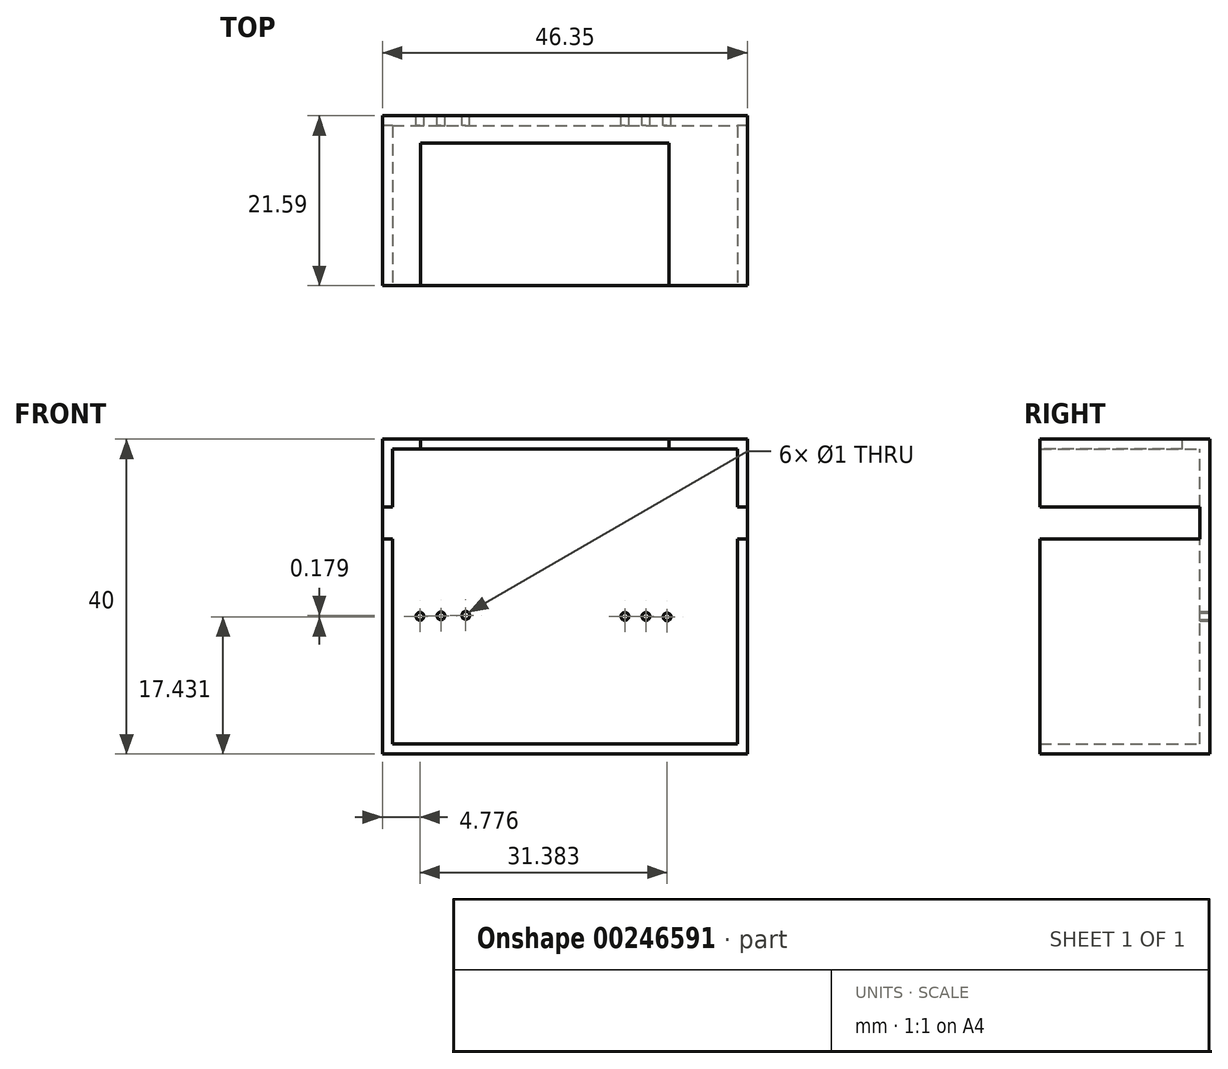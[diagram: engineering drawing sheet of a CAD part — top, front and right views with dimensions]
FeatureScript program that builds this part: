
annotation { "Feature Type Name" : "Feature", "Feature Type Description" : "" }
export const myFeature = defineFeature(function(context is Context, id is Id, definition is map)
    precondition{}
    {
        {
            var Q0;
            Q0=qCreatedBy(makeId("Front.planeOp"),FACE);
            var sketch = newSketch(context, id + "F0", { "sketchPlane" : qUnion([Q0])});
            skLineSegment(sketch, "E0.bottom", {"start": v(0, 0) * mm, "end": v(46.35, 0) * mm});
            skLineSegment(sketch, "E0.top", {"start": v(0, 40) * mm, "end": v(46.35, 40) * mm});
            skLineSegment(sketch, "E0.left", {"start": v(0, 0) * mm, "end": v(0, 40) * mm});
            skLineSegment(sketch, "E0.right", {"start": v(46.35, 0) * mm, "end": v(46.35, 40) * mm});
            skSolve(sketch);
        }
        {
            var Q0;
            Q0 = qSketchRegion(id + "F0", true);
            extrude(context, id + "F1", {"entities" : qUnion([Q0]), "depth" : 21.59 * mm});
        }
        {
            var Q0;
            Q0=makeQuery(id+"F1.opExtrude","CAP_FACE",FACE,{"disambiguationData":[OSD([sQuery(id+"F0.wireOp",EDGE,"E0.bottom"),sQuery(id+"F0.wireOp",EDGE,"E0.top"),sQuery(id+"F0.wireOp",EDGE,"E0.left"),sQuery(id+"F0.wireOp",EDGE,"E0.right")])],"isStart":true});
            var sketch = newSketch(context, id + "F2", { "sketchPlane" : qUnion([Q0])});
            skSolve(sketch);
        }
        {
            var Q0;
            Q0=makeQuery(id+"F1.opExtrude","CAP_FACE",FACE,{"disambiguationData":[OSD([sQuery(id+"F0.wireOp",EDGE,"E0.bottom"),sQuery(id+"F0.wireOp",EDGE,"E0.top"),sQuery(id+"F0.wireOp",EDGE,"E0.left"),sQuery(id+"F0.wireOp",EDGE,"E0.right")])],"isStart":false});
            shell(context, id + "F3", {"entities" : qUnion([Q0]), "thickness" : 1.27 * mm});
        }
        {
            var Q0;
            Q0=makeQuery(id+"F2.imprint","IMPRINT",FACE,{"disambiguationData":[TD([[makeQuery(id+"F2.imprint","IMPRINT",EDGE,{"derivedFrom":makeQuery(id+"F1.opExtrude","CAP_EDGE",EDGE,{"disambiguationData":[OSD([sQuery(id+"F0.wireOp",EDGE,"E0.bottom")])],"isStart":true})}),-1.0]])]});
            var sketch = newSketch(context, id + "F4", { "sketchPlane" : qUnion([Q0])});
            skPoint(sketch, "E1", {"position": v(-20.64, 22.54) * mm});
            skSolve(sketch);
        }
        {
            var Q0;
            Q0=qCreatedBy(makeId("Right.planeOp"),FACE);
            var sketch = newSketch(context, id + "F5", { "sketchPlane" : qUnion([Q0])});
            skLineSegment(sketch, "E2.bottom", {"start": v(-1.27, 31.4) * mm, "end": v(-28.2, 31.4) * mm});
            skLineSegment(sketch, "E2.top", {"start": v(-1.27, 27.34) * mm, "end": v(-28.2, 27.34) * mm});
            skLineSegment(sketch, "E2.left", {"start": v(-1.27, 31.4) * mm, "end": v(-1.27, 27.34) * mm});
            skLineSegment(sketch, "E2.right", {"start": v(-28.2, 31.4) * mm, "end": v(-28.2, 27.34) * mm});
            skSolve(sketch);
        }
        {
            var Q0;
            Q0=makeQuery(id+"F5.imprint","IMPRINT",FACE,{"disambiguationData":[TD([[makeQuery(id+"F5.imprint","IMPRINT",EDGE,{"derivedFrom":sQuery(id+"F5.wireOp",EDGE,"E2.bottom")}),1.0]])]});
            extrude(context, id + "F6", {"entities" : qUnion([Q0]), "operationType" : NewBodyOperationType.REMOVE, "depth" : 63.25 * mm});
        }
        {
            var Q0;
            Q0=makeQuery(id+"F4.imprint","IMPRINT",FACE,{"disambiguationData":[TD([[makeQuery(id+"F4.imprint","IMPRINT",EDGE,{"derivedFrom":makeQuery(id+"F2.imprint","IMPRINT",EDGE,{"derivedFrom":makeQuery(id+"F1.opExtrude","CAP_EDGE",EDGE,{"disambiguationData":[OSD([sQuery(id+"F0.wireOp",EDGE,"E0.bottom")])],"isStart":true})})}),-1.0]])]});
            var sketch = newSketch(context, id + "F7", { "sketchPlane" : qUnion([Q0])});
            skPoint(sketch, "E3", {"position": v(-10.6, 17.6) * mm});
            skSolve(sketch);
        }
        {
            var Q0;
            Q0=sQuery(id+"F7.wireOp",VERTEX,"E3");
            var Q1;
            Q1=makeQuery(id+"F1.opExtrude","SWEPT_BODY",BODY,{"disambiguationData":[OSD([sQuery(id+"F0.wireOp",EDGE,"E0.bottom"),sQuery(id+"F0.wireOp",EDGE,"E0.top"),sQuery(id+"F0.wireOp",EDGE,"E0.left"),sQuery(id+"F0.wireOp",EDGE,"E0.right")])]});
            hole(context, id + "F8", {"style" : HoleStyle.SIMPLE, "endStyle" : HoleEndStyle.THROUGH, "holeDiameter" : 1 * mm, "tappedDepth" : 12.7 * mm, "tapClearance" : 3, "locations" : qUnion([Q0]), "scope" : qUnion([Q1])});
        }
        {
            var Q0;
            Q0=makeQuery(id+"F4.imprint","IMPRINT",FACE,{"disambiguationData":[TD([[makeQuery(id+"F4.imprint","IMPRINT",EDGE,{"derivedFrom":makeQuery(id+"F2.imprint","IMPRINT",EDGE,{"derivedFrom":makeQuery(id+"F1.opExtrude","CAP_EDGE",EDGE,{"disambiguationData":[OSD([sQuery(id+"F0.wireOp",EDGE,"E0.bottom")])],"isStart":true})})}),-1.0]])]});
            var sketch = newSketch(context, id + "F9", { "sketchPlane" : qUnion([Q0])});
            skPoint(sketch, "E4", {"position": v(-30.81, 17.5) * mm});
            skSolve(sketch);
        }
        {
            var Q0;
            Q0=sQuery(id+"F9.wireOp",VERTEX,"E4");
            var Q1;
            Q1=makeQuery(id+"F1.opExtrude","SWEPT_BODY",BODY,{"disambiguationData":[OSD([sQuery(id+"F0.wireOp",EDGE,"E0.bottom"),sQuery(id+"F0.wireOp",EDGE,"E0.top"),sQuery(id+"F0.wireOp",EDGE,"E0.left"),sQuery(id+"F0.wireOp",EDGE,"E0.right")])]});
            hole(context, id + "F10", {"style" : HoleStyle.SIMPLE, "endStyle" : HoleEndStyle.THROUGH, "holeDiameter" : 1 * mm, "tappedDepth" : 12.7 * mm, "tapClearance" : 3, "locations" : qUnion([Q0]), "scope" : qUnion([Q1])});
        }
        {
            var Q0;
            Q0=makeQuery(id+"F4.imprint","IMPRINT",FACE,{"disambiguationData":[TD([[makeQuery(id+"F4.imprint","IMPRINT",EDGE,{"derivedFrom":makeQuery(id+"F2.imprint","IMPRINT",EDGE,{"derivedFrom":makeQuery(id+"F1.opExtrude","CAP_EDGE",EDGE,{"disambiguationData":[OSD([sQuery(id+"F0.wireOp",EDGE,"E0.bottom")])],"isStart":true})})}),-1.0]])]});
            var sketch = newSketch(context, id + "F11", { "sketchPlane" : qUnion([Q0])});
            skPoint(sketch, "E5", {"position": v(-33.49, 17.5) * mm});
            skSolve(sketch);
        }
        {
            var Q0;
            Q0=sQuery(id+"F11.wireOp",VERTEX,"E5");
            var Q1;
            Q1=makeQuery(id+"F1.opExtrude","SWEPT_BODY",BODY,{"disambiguationData":[OSD([sQuery(id+"F0.wireOp",EDGE,"E0.bottom"),sQuery(id+"F0.wireOp",EDGE,"E0.top"),sQuery(id+"F0.wireOp",EDGE,"E0.left"),sQuery(id+"F0.wireOp",EDGE,"E0.right")])]});
            hole(context, id + "F12", {"style" : HoleStyle.SIMPLE, "endStyle" : HoleEndStyle.THROUGH, "holeDiameter" : 1 * mm, "tappedDepth" : 12.7 * mm, "tapClearance" : 3, "locations" : qUnion([Q0]), "scope" : qUnion([Q1])});
        }
        {
            var Q0;
            Q0=makeQuery(id+"F4.imprint","IMPRINT",FACE,{"disambiguationData":[TD([[makeQuery(id+"F4.imprint","IMPRINT",EDGE,{"derivedFrom":makeQuery(id+"F2.imprint","IMPRINT",EDGE,{"derivedFrom":makeQuery(id+"F1.opExtrude","CAP_EDGE",EDGE,{"disambiguationData":[OSD([sQuery(id+"F0.wireOp",EDGE,"E0.bottom")])],"isStart":true})})}),-1.0]])]});
            var sketch = newSketch(context, id + "F13", { "sketchPlane" : qUnion([Q0])});
            skPoint(sketch, "E6", {"position": v(-36.16, 17.43) * mm});
            skSolve(sketch);
        }
        {
            var Q0;
            Q0=sQuery(id+"F13.wireOp",VERTEX,"E6");
            var Q1;
            Q1=makeQuery(id+"F1.opExtrude","SWEPT_BODY",BODY,{"disambiguationData":[OSD([sQuery(id+"F0.wireOp",EDGE,"E0.bottom"),sQuery(id+"F0.wireOp",EDGE,"E0.top"),sQuery(id+"F0.wireOp",EDGE,"E0.left"),sQuery(id+"F0.wireOp",EDGE,"E0.right")])]});
            hole(context, id + "F14", {"style" : HoleStyle.SIMPLE, "endStyle" : HoleEndStyle.THROUGH, "holeDiameter" : 1 * mm, "tappedDepth" : 12.7 * mm, "tapClearance" : 3, "locations" : qUnion([Q0]), "scope" : qUnion([Q1])});
        }
        {
            var Q0;
            Q0=makeQuery(id+"F4.imprint","IMPRINT",FACE,{"disambiguationData":[TD([[makeQuery(id+"F4.imprint","IMPRINT",EDGE,{"derivedFrom":makeQuery(id+"F2.imprint","IMPRINT",EDGE,{"derivedFrom":makeQuery(id+"F1.opExtrude","CAP_EDGE",EDGE,{"disambiguationData":[OSD([sQuery(id+"F0.wireOp",EDGE,"E0.bottom")])],"isStart":true})})}),-1.0]])]});
            var sketch = newSketch(context, id + "F15", { "sketchPlane" : qUnion([Q0])});
            skPoint(sketch, "E7", {"position": v(-7.45, 17.57) * mm});
            skSolve(sketch);
        }
        {
            var Q0;
            Q0=sQuery(id+"F15.wireOp",VERTEX,"E7");
            var Q1;
            Q1=makeQuery(id+"F1.opExtrude","SWEPT_BODY",BODY,{"disambiguationData":[OSD([sQuery(id+"F0.wireOp",EDGE,"E0.bottom"),sQuery(id+"F0.wireOp",EDGE,"E0.top"),sQuery(id+"F0.wireOp",EDGE,"E0.left"),sQuery(id+"F0.wireOp",EDGE,"E0.right")])]});
            hole(context, id + "F16", {"style" : HoleStyle.SIMPLE, "endStyle" : HoleEndStyle.THROUGH, "holeDiameter" : 1 * mm, "tappedDepth" : 12.7 * mm, "tapClearance" : 3, "locations" : qUnion([Q0]), "scope" : qUnion([Q1])});
        }
        {
            var Q0;
            Q0=makeQuery(id+"F4.imprint","IMPRINT",FACE,{"disambiguationData":[TD([[makeQuery(id+"F4.imprint","IMPRINT",EDGE,{"derivedFrom":makeQuery(id+"F2.imprint","IMPRINT",EDGE,{"derivedFrom":makeQuery(id+"F1.opExtrude","CAP_EDGE",EDGE,{"disambiguationData":[OSD([sQuery(id+"F0.wireOp",EDGE,"E0.bottom")])],"isStart":true})})}),-1.0]])]});
            var sketch = newSketch(context, id + "F17", { "sketchPlane" : qUnion([Q0])});
            skPoint(sketch, "E8", {"position": v(-4.78, 17.5) * mm});
            skSolve(sketch);
        }
        {
            var Q0;
            Q0=makeQuery(id+"F1.opExtrude","SWEPT_FACE",FACE,{"disambiguationData":[OSD([sQuery(id+"F0.wireOp",EDGE,"E0.top")])]});
            var sketch = newSketch(context, id + "F18", { "sketchPlane" : qUnion([Q0])});
            skLineSegment(sketch, "E9.bottom", {"start": v(4.86, -3.47) * mm, "end": v(36.39, -3.47) * mm});
            skLineSegment(sketch, "E9.top", {"start": v(4.86, -21.59) * mm, "end": v(36.39, -21.59) * mm});
            skLineSegment(sketch, "E9.left", {"start": v(4.86, -3.47) * mm, "end": v(4.86, -21.59) * mm});
            skLineSegment(sketch, "E9.right", {"start": v(36.39, -3.47) * mm, "end": v(36.39, -21.59) * mm});
            skSolve(sketch);
        }
        {
            var Q0;
            Q0 = qSketchRegion(id + "F18", true);
            extrude(context, id + "F19", {"entities" : qUnion([Q0]), "operationType" : NewBodyOperationType.REMOVE, "oppositeDirection" : true, "depth" : 25.4 * mm});
        }
        {
            var Q0;
            Q0=sQuery(id+"F17.wireOp",VERTEX,"E8");
            var Q1;
            Q1=makeQuery(id+"F1.opExtrude","SWEPT_BODY",BODY,{"disambiguationData":[OSD([sQuery(id+"F0.wireOp",EDGE,"E0.bottom"),sQuery(id+"F0.wireOp",EDGE,"E0.top"),sQuery(id+"F0.wireOp",EDGE,"E0.left"),sQuery(id+"F0.wireOp",EDGE,"E0.right")])]});
            hole(context, id + "F20", {"style" : HoleStyle.SIMPLE, "endStyle" : HoleEndStyle.THROUGH, "holeDiameter" : 1 * mm, "tappedDepth" : 12.7 * mm, "tapClearance" : 3, "locations" : qUnion([Q0]), "scope" : qUnion([Q1])});
        }
    });
